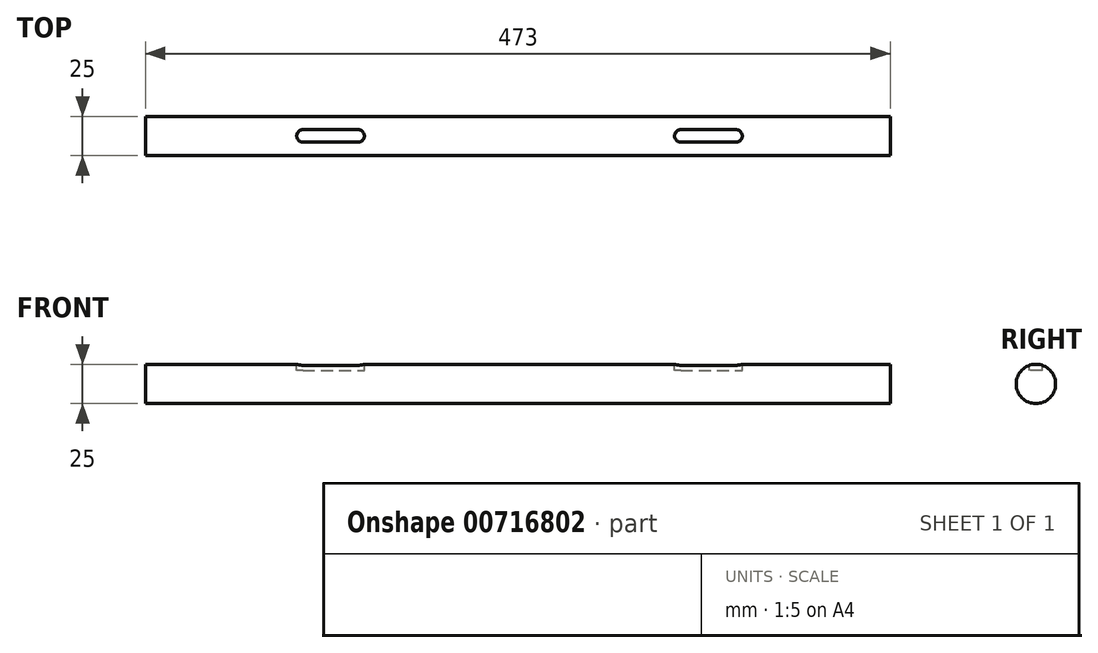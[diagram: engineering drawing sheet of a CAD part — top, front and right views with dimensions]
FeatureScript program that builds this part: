
annotation { "Feature Type Name" : "Feature", "Feature Type Description" : "" }
export const myFeature = defineFeature(function(context is Context, id is Id, definition is map)
    precondition{}
    {
        {
            var Q0;
            Q0=qCreatedBy(makeId("Right.planeOp"),FACE);
            var sketch = newSketch(context, id + "F0", { "sketchPlane" : qUnion([Q0])});
            skCircle(sketch, "E0", {"center": v(0, 0) * mm, "radius": 12.5 * mm});
            skSolve(sketch);
        }
        {
            var Q0;
            Q0=qCreatedBy(makeId("Top.planeOp"),FACE);
            cPlane(context, id + "F1", {"entities" : qUnion([Q0]), "cplaneType" : CPlaneType.OFFSET, "offset" : 12.5 * mm, "width" : 150 * mm, "height" : 150 * mm});
        }
        {
            var Q0;
            Q0 = qSketchRegion(id + "F0", true);
            extrude(context, id + "F2", {"entities" : qUnion([Q0]), "endBound" : BoundingType.SYMMETRIC, "depth" : 473 * mm, "offsetDistance" : 25 * mm});
        }
        {
            var Q0;
            Q0=qCreatedBy(id+"F1.planeOp",FACE);
            var sketch = newSketch(context, id + "F3", { "sketchPlane" : qUnion([Q0])});
            skLineSegment(sketch, "E1", {"start": v(-136.5, 0) * mm, "end": v(-101.5, 0) * mm});
            skLineSegment(sketch, "E2", {"start": v(103.5, 0) * mm, "end": v(138.5, 0) * mm});
            skArc(sketch, "E3.0.startCap", {"start": v(-136.5, -4) * mm, "mid": v(-140.5, 0) * mm, "end": v(-136.5, 4) * mm});
            skArc(sketch, "E3.0.endCap", {"start": v(-101.5, 4) * mm, "mid": v(-97.5, 0) * mm, "end": v(-101.5, -4) * mm});
            skLineSegment(sketch, "E3.0.left", {"start": v(-136.5, 4) * mm, "end": v(-101.5, 4) * mm});
            skLineSegment(sketch, "E3.0.right", {"start": v(-136.5, -4) * mm, "end": v(-101.5, -4) * mm});
            skArc(sketch, "E3.1.startCap", {"start": v(103.5, -4) * mm, "mid": v(99.5, 0) * mm, "end": v(103.5, 4) * mm});
            skArc(sketch, "E3.1.endCap", {"start": v(138.5, 4) * mm, "mid": v(142.5, 0) * mm, "end": v(138.5, -4) * mm});
            skLineSegment(sketch, "E3.1.left", {"start": v(103.5, 4) * mm, "end": v(138.5, 4) * mm});
            skLineSegment(sketch, "E3.1.right", {"start": v(103.5, -4) * mm, "end": v(138.5, -4) * mm});
            skSolve(sketch);
        }
        {
            var Q0;
            Q0 = qSketchRegion(id + "F3", true);
            extrude(context, id + "F4", {"entities" : qUnion([Q0]), "operationType" : NewBodyOperationType.REMOVE, "oppositeDirection" : true, "depth" : 4 * mm, "offsetDistance" : 25 * mm});
        }
    });
